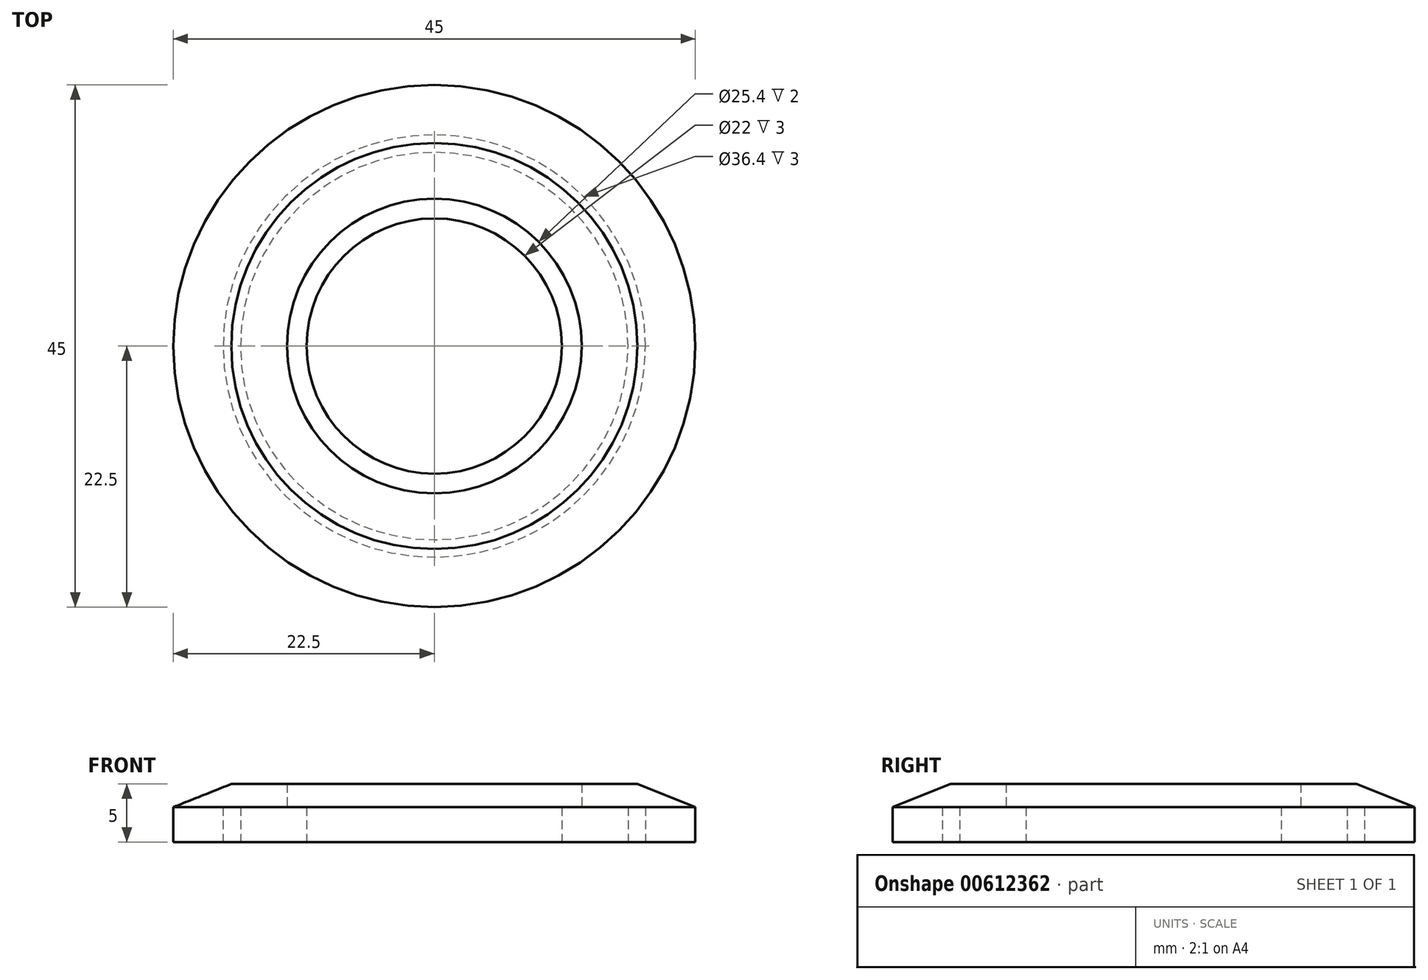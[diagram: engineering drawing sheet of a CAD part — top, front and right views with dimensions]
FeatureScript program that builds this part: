
annotation { "Feature Type Name" : "Feature", "Feature Type Description" : "" }
export const myFeature = defineFeature(function(context is Context, id is Id, definition is map)
    precondition{}
    {
        {
            var Q0;
            Q0=qCreatedBy(makeId("Front.planeOp"),FACE);
            var sketch = newSketch(context, id + "F0", { "sketchPlane" : qUnion([Q0])});
            skLineSegment(sketch, "E0", {"start": v(0, 0) * mm, "end": v(0, 7.87) * mm});
            skLineSegment(sketch, "E1", {"start": v(11, 0) * mm, "end": v(16.7, 0) * mm});
            skLineSegment(sketch, "E2", {"start": v(22.5, 0) * mm, "end": v(22.5, 3) * mm});
            skLineSegment(sketch, "E3", {"start": v(22.5, 3) * mm, "end": v(17.5, 5) * mm});
            skLineSegment(sketch, "E4", {"start": v(17.5, 5) * mm, "end": v(12.7, 5) * mm});
            skLineSegment(sketch, "E5", {"start": v(12.7, 5) * mm, "end": v(12.7, 3) * mm});
            skLineSegment(sketch, "E6", {"start": v(12.7, 3) * mm, "end": v(11, 3) * mm});
            skLineSegment(sketch, "E7", {"start": v(11, 3) * mm, "end": v(11, 0) * mm});
            skLineSegment(sketch, "E8.top", {"start": v(16.7, 3) * mm, "end": v(18.2, 3) * mm});
            skLineSegment(sketch, "E8.left", {"start": v(16.7, 0) * mm, "end": v(16.7, 3) * mm});
            skLineSegment(sketch, "E8.right", {"start": v(18.2, 0) * mm, "end": v(18.2, 3) * mm});
            skLineSegment(sketch, "E9.trimOffspring", {"start": v(18.2, 0) * mm, "end": v(22.5, 0) * mm});
            skSolve(sketch);
        }
        {
            var Q0;
            Q0=makeQuery(id+"F0.imprint","IMPRINT",FACE,{"disambiguationData":[TD([[makeQuery(id+"F0.imprint","IMPRINT",EDGE,{"derivedFrom":sQuery(id+"F0.wireOp",EDGE,"E1")}),1.0]])]});
            var Q1;
            Q1=sQuery(id+"F0.wireOp",EDGE,"E0");
            revolve(context, id + "F1", {"entities" : qUnion([Q0]), "axis" : qUnion([Q1]), "revolveType" : RevolveType.FULL});
        }
    });
